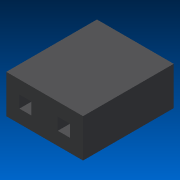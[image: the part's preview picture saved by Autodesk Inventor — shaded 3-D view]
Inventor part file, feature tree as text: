
AUTODESK INVENTOR PART (.ipt)
format: ipt  version: 2015 SP1 (Build 190203100, 203)  size: 89,600 bytes
history: native  units: mm
features: extrude x2, sketch x2, other x1
ambient origin geometry x8: Origin, YZ Plane, XZ Plane, XY Plane, X Axis, Y Axis, Z Axis, Center Point
bodies: Body1 (feature_tree)
feature tree (5):
  other  "Твердое тело1"
  extrude  "Выдавливание1"  Depth=5.08mm
  extrude  "Выдавливание2"  Depth=2.54mm
  sketch  "Эскиз1"
  sketch  "Эскиз2"
